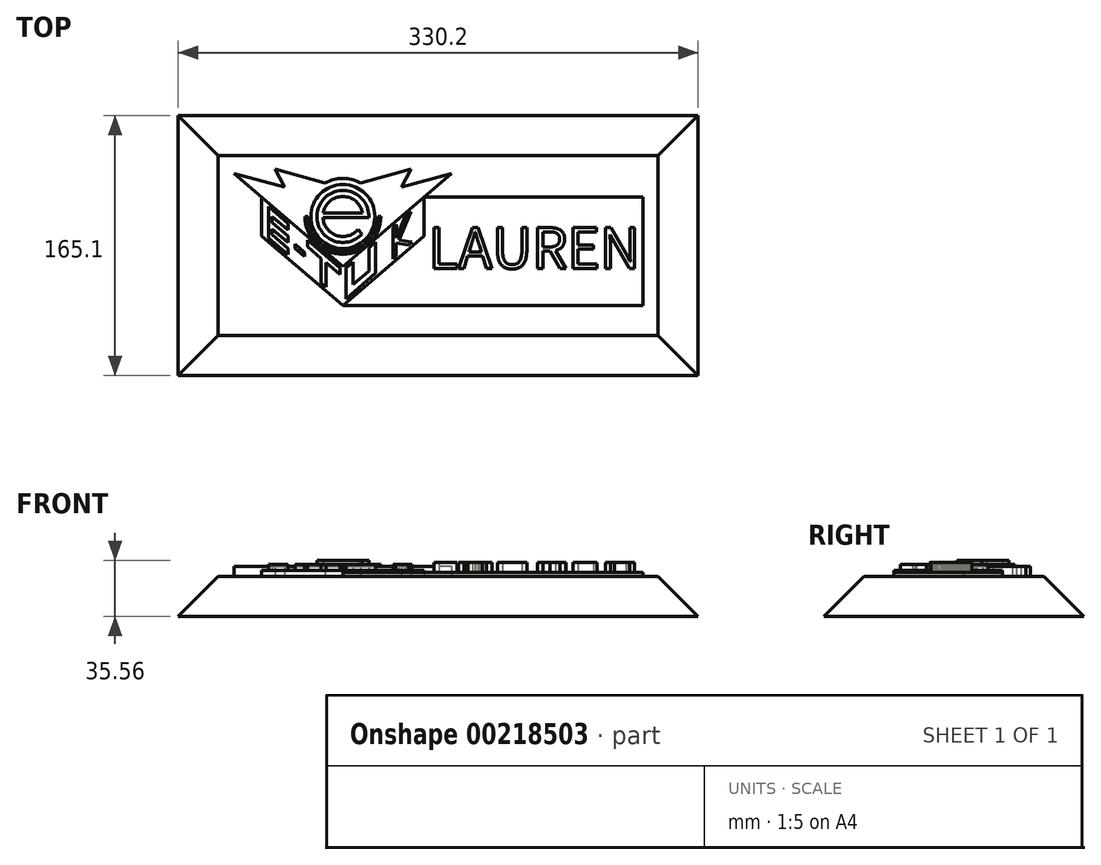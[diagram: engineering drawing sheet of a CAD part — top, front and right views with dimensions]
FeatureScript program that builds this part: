
annotation { "Feature Type Name" : "Feature", "Feature Type Description" : "" }
export const myFeature = defineFeature(function(context is Context, id is Id, definition is map)
    precondition{}
    {
        {
            var Q0;
            Q0=qCreatedBy(makeId("Top.planeOp"),FACE);
            var sketch = newSketch(context, id + "F0", { "sketchPlane" : qUnion([Q0])});
            skArc(sketch, "E0", {"start": v(12.53, 2.07) * mm, "mid": v(0, 12.7) * mm, "end": v(-12.53, 2.07) * mm});
            skArc(sketch, "E1", {"start": v(16.5, -0.78) * mm, "mid": v(-15.23, 6.37) * mm, "end": v(12.14, -11.18) * mm});
            skLineSegment(sketch, "E2", {"start": v(12.7, -0.78) * mm, "end": v(-12.68, -0.78) * mm});
            skLineSegment(sketch, "E3", {"start": v(-12.68, -0.78) * mm, "end": v(16.5, -0.78) * mm});
            skLineSegment(sketch, "E4", {"start": v(9.59, -8.33) * mm, "end": v(12.14, -11.18) * mm});
            skArc(sketch, "E5.trimOffspring", {"start": v(-12.68, -0.78) * mm, "mid": v(-4.08, -12.03) * mm, "end": v(9.59, -8.33) * mm});
            skLineSegment(sketch, "E6", {"start": v(-12.53, 2.07) * mm, "end": v(12.53, 2.07) * mm});
            skSolve(sketch);
        }
        {
            var Q0;
            Q0=makeQuery(id+"F0.imprint","IMPRINT",FACE,{"disambiguationData":[TD([[makeQuery(id+"F0.imprint","IMPRINT",EDGE,{"derivedFrom":sQuery(id+"F0.wireOp",EDGE,"E0")}),-1.0]])]});
            extrude(context, id + "F1", {"entities" : qUnion([Q0]), "depth" : 10.16 * mm});
        }
        {
            var Q0;
            Q0=qCreatedBy(makeId("Top.planeOp"),FACE);
            var sketch = newSketch(context, id + "F2", { "sketchPlane" : qUnion([Q0])});
            skCircle(sketch, "E7", {"center": v(0, 0) * mm, "radius": 20.32 * mm});
            skSolve(sketch);
        }
        {
            var Q0;
            Q0=qSketchRegion(id+"F2",true);
            extrude(context, id + "F3", {"entities" : qUnion([Q0]), "operationType" : NewBodyOperationType.ADD, "depth" : 7.62 * mm});
        }
        {
            var Q0;
            Q0=qCreatedBy(makeId("Top.planeOp"),FACE);
            var sketch = newSketch(context, id + "F4", { "sketchPlane" : qUnion([Q0])});
            skLineSegment(sketch, "E8", {"start": v(-69.02, 27.27) * mm, "end": v(-37.13, 18.72) * mm});
            skLineSegment(sketch, "E9", {"start": v(-37.13, 18.72) * mm, "end": v(-43.14, 30.14) * mm});
            skLineSegment(sketch, "E10", {"start": v(-43.14, 30.14) * mm, "end": v(-11.32, 21.31) * mm});
            skLineSegment(sketch, "E11", {"start": v(-69.02, 27.27) * mm, "end": v(0, -31.75) * mm});
            skLineSegment(sketch, "E12.MirrorCS", {"start": v(43.14, 30.14) * mm, "end": v(11.32, 21.31) * mm});
            skLineSegment(sketch, "E13.MirrorCS", {"start": v(69.02, 27.27) * mm, "end": v(0, -31.75) * mm});
            skLineSegment(sketch, "E14.MirrorCS", {"start": v(69.02, 27.27) * mm, "end": v(37.13, 18.72) * mm});
            skLineSegment(sketch, "E15.MirrorCS", {"start": v(37.13, 18.72) * mm, "end": v(43.14, 30.14) * mm});
            skArc(sketch, "E16.trimOffspring", {"start": v(11.32, 21.31) * mm, "mid": v(0, 24.13) * mm, "end": v(-11.32, 21.31) * mm});
            skSolve(sketch);
        }
        {
            var Q0;
            Q0=qSketchRegion(id+"F4",true);
            var Q1;
            Q1=makeQuery(id+"F2.imprint","IMPRINT",FACE,{"disambiguationData":[TD([[makeQuery(id+"F2.imprint","IMPRINT",EDGE,{"derivedFrom":sQuery(id+"F2.wireOp",EDGE,"E7")}),1.0]])]});
            extrude(context, id + "F5", {"entities" : qUnion([Q0, Q1]), "operationType" : NewBodyOperationType.ADD, "depth" : 6.35 * mm});
        }
        {
            var Q0;
            Q0=qCreatedBy(makeId("Top.planeOp"),FACE);
            var sketch = newSketch(context, id + "F6", { "sketchPlane" : qUnion([Q0])});
            skLineSegment(sketch, "E17", {"start": v(-51.6, -12.38) * mm, "end": v(0, -56.51) * mm});
            skLineSegment(sketch, "E18", {"start": v(0, -56.51) * mm, "end": v(51.6, -12.38) * mm});
            skLineSegment(sketch, "E19", {"start": v(-51.6, 12.38) * mm, "end": v(-51.6, -12.38) * mm});
            skLineSegment(sketch, "E20", {"start": v(51.6, 12.38) * mm, "end": v(51.6, -12.38) * mm});
            skLineSegment(sketch, "E21", {"start": v(-51.6, 12.38) * mm, "end": v(0, -31.75) * mm});
            skLineSegment(sketch, "E22", {"start": v(0, -31.75) * mm, "end": v(51.6, 12.38) * mm});
            skSolve(sketch);
        }
        {
            var Q0;
            Q0=qSketchRegion(id+"F6",true);
            extrude(context, id + "F7", {"entities" : qUnion([Q0]), "operationType" : NewBodyOperationType.ADD, "depth" : 3.8 * mm});
        }
        {
            var Q0;
            Q0=makeQuery(id+"F7.opExtrude","CAP_FACE",FACE,{"disambiguationData":[OSD([sQuery(id+"F6.wireOp",EDGE,"E17"),sQuery(id+"F6.wireOp",EDGE,"E18"),sQuery(id+"F6.wireOp",EDGE,"E19"),sQuery(id+"F6.wireOp",EDGE,"E20"),sQuery(id+"F6.wireOp",EDGE,"E21"),sQuery(id+"F6.wireOp",EDGE,"E22")])],"isStart":false});
            var sketch = newSketch(context, id + "F8", { "sketchPlane" : qUnion([Q0])});
            skPoint(sketch, "E23.startSnap0", {"position": v(-51.6, 0) * mm});
            skLineSegment(sketch, "E24", {"start": v(-51.6, -9.87) * mm, "end": v(-51.6, 9.87) * mm, "construction": true});
            skLineSegment(sketch, "E25", {"start": v(-47.26, 6.16) * mm, "end": v(-34.74, -4.55) * mm});
            skLineSegment(sketch, "E26", {"start": v(-34.74, -4.55) * mm, "end": v(-34.74, -8.63) * mm});
            skLineSegment(sketch, "E27", {"start": v(-34.74, -8.63) * mm, "end": v(-44.83, 0) * mm});
            skLineSegment(sketch, "E28", {"start": v(-44.83, 0) * mm, "end": v(-44.83, -3.75) * mm});
            skLineSegment(sketch, "E29", {"start": v(-44.83, -3.75) * mm, "end": v(-34.74, -12.38) * mm});
            skLineSegment(sketch, "E30", {"start": v(-34.74, -12.38) * mm, "end": v(-34.74, -16.46) * mm});
            skLineSegment(sketch, "E31", {"start": v(-34.74, -16.46) * mm, "end": v(-44.83, -7.83) * mm});
            skLineSegment(sketch, "E32", {"start": v(-44.83, -7.83) * mm, "end": v(-44.83, -11.58) * mm});
            skLineSegment(sketch, "E33", {"start": v(-44.83, -11.58) * mm, "end": v(-34.74, -20.21) * mm});
            skLineSegment(sketch, "E34", {"start": v(-34.74, -20.21) * mm, "end": v(-34.74, -24.3) * mm});
            skLineSegment(sketch, "E35", {"start": v(-34.74, -24.3) * mm, "end": v(-47.26, -13.59) * mm});
            skLineSegment(sketch, "E36", {"start": v(-47.26, 6.16) * mm, "end": v(-47.26, -13.59) * mm});
            skLineSegment(sketch, "E37", {"start": v(-30.38, -20.21) * mm, "end": v(-30.38, -17.65) * mm});
            skLineSegment(sketch, "E38", {"start": v(-30.38, -17.65) * mm, "end": v(-24.17, -22.96) * mm});
            skLineSegment(sketch, "E39", {"start": v(-24.17, -22.96) * mm, "end": v(-24.17, -25.53) * mm});
            skLineSegment(sketch, "E40", {"start": v(-24.17, -25.53) * mm, "end": v(-30.38, -20.21) * mm});
            skLineSegment(sketch, "E41", {"start": v(-22.38, -15.12) * mm, "end": v(-1.9, -32.63) * mm});
            skLineSegment(sketch, "E42", {"start": v(-1.9, -32.63) * mm, "end": v(-1.9, -36.71) * mm});
            skLineSegment(sketch, "E43", {"start": v(-1.9, -36.71) * mm, "end": v(-10.6, -29.28) * mm});
            skLineSegment(sketch, "E44", {"start": v(-10.6, -29.28) * mm, "end": v(-10.6, -44.95) * mm});
            skLineSegment(sketch, "E45", {"start": v(-10.6, -44.95) * mm, "end": v(-13.7, -42.3) * mm});
            skLineSegment(sketch, "E46", {"start": v(-13.7, -42.3) * mm, "end": v(-13.7, -26.63) * mm});
            skLineSegment(sketch, "E47", {"start": v(-13.7, -26.63) * mm, "end": v(-22.38, -19.2) * mm});
            skLineSegment(sketch, "E48", {"start": v(-22.38, -19.2) * mm, "end": v(-22.38, -15.12) * mm});
            skLineSegment(sketch, "E49", {"start": v(1.9, -32.62) * mm, "end": v(6.3, -28.86) * mm});
            skLineSegment(sketch, "E50", {"start": v(6.3, -28.86) * mm, "end": v(6.3, -43.26) * mm});
            skLineSegment(sketch, "E51", {"start": v(6.3, -43.26) * mm, "end": v(16.5, -34.54) * mm});
            skLineSegment(sketch, "E52", {"start": v(16.5, -34.54) * mm, "end": v(16.5, -20.14) * mm});
            skLineSegment(sketch, "E53", {"start": v(16.5, -20.14) * mm, "end": v(20.85, -16.3) * mm});
            skLineSegment(sketch, "E54", {"start": v(20.85, -16.3) * mm, "end": v(20.85, -36.06) * mm});
            skLineSegment(sketch, "E55", {"start": v(20.85, -36.06) * mm, "end": v(1.9, -52.37) * mm});
            skLineSegment(sketch, "E56", {"start": v(1.9, -52.37) * mm, "end": v(1.9, -32.62) * mm});
            skLineSegment(sketch, "E57", {"start": v(31.73, -7.12) * mm, "end": v(31.73, -27.15) * mm});
            skLineSegment(sketch, "E58", {"start": v(31.73, -27.15) * mm, "end": v(33.91, -25.22) * mm});
            skLineSegment(sketch, "E59", {"start": v(33.91, -25.22) * mm, "end": v(33.91, -16.82) * mm});
            skLineSegment(sketch, "E60", {"start": v(33.94, -13.64) * mm, "end": v(33.94, -5.23) * mm});
            skLineSegment(sketch, "E61", {"start": v(33.94, -5.23) * mm, "end": v(31.73, -7.12) * mm});
            skLineSegment(sketch, "E62", {"start": v(41.79, -18.27) * mm, "end": v(44, -16.38) * mm});
            skLineSegment(sketch, "E63", {"start": v(33.94, -13.64) * mm, "end": v(39.5, 0) * mm});
            skLineSegment(sketch, "E64", {"start": v(33.91, -16.82) * mm, "end": v(41.79, -18.27) * mm});
            skLineSegment(sketch, "E65", {"start": v(44, -16.38) * mm, "end": v(35.85, -14.87) * mm});
            skLineSegment(sketch, "E66", {"start": v(35.85, -14.87) * mm, "end": v(43.2, 3.16) * mm});
            skLineSegment(sketch, "E67", {"start": v(39.5, 0) * mm, "end": v(43.2, 3.16) * mm});
            skSolve(sketch);
        }
        {
            var Q0;
            Q0=qSketchRegion(id+"F8",true);
            extrude(context, id + "F9", {"entities" : qUnion([Q0]), "operationType" : NewBodyOperationType.ADD, "depth" : 3.8 * mm});
        }
        {
            var Q0;
            Q0=makeQuery(id+"F5.boolean.opBoolean","MERGE",FACE,{"derivedFrom":[makeQuery(id+"F5.opExtrude","CAP_FACE",FACE,{"disambiguationData":[OSD([sQuery(id+"F2.wireOp",EDGE,"E7")])],"isStart":false}),makeQuery(id+"F5.opExtrude","CAP_FACE",FACE,{"disambiguationData":[OSD([sQuery(id+"F4.wireOp",EDGE,"E8"),sQuery(id+"F4.wireOp",EDGE,"E9"),sQuery(id+"F4.wireOp",EDGE,"E10"),sQuery(id+"F4.wireOp",EDGE,"E11"),sQuery(id+"F4.wireOp",EDGE,"E13.MirrorCS"),sQuery(id+"F4.wireOp",EDGE,"E14.MirrorCS"),sQuery(id+"F4.wireOp",EDGE,"E12.MirrorCS"),sQuery(id+"F4.wireOp",EDGE,"E15.MirrorCS"),sQuery(id+"F4.wireOp",EDGE,"E16.trimOffspring")])],"isStart":false})]});
            var sketch = newSketch(context, id + "F10", { "sketchPlane" : qUnion([Q0])});
            skArc(sketch, "E68", {"start": v(-24.13, 0) * mm, "mid": v(0, -24.13) * mm, "end": v(24.13, 0) * mm});
            skArc(sketch, "E69", {"start": v(-22.23, 0) * mm, "mid": v(0, -22.23) * mm, "end": v(22.23, 0) * mm});
            skLineSegment(sketch, "E70", {"start": v(-24.13, 0) * mm, "end": v(-22.23, 0) * mm});
            skLineSegment(sketch, "E71", {"start": v(24.13, 0) * mm, "end": v(22.23, 0) * mm});
            skSolve(sketch);
        }
        {
            var Q0;
            Q0=qSketchRegion(id+"F10",true);
            extrude(context, id + "F11", {"entities" : qUnion([Q0]), "operationType" : NewBodyOperationType.ADD, "depth" : 1.27 * mm});
        }
        {
            var Q0;
            {var subQ0=sQuery(id+"F2.wireOp",EDGE,"E7");Q0=makeQuery(id+"F7.boolean.opBoolean","MERGE",FACE,{"derivedFrom":[makeQuery(id+"F5.boolean.opBoolean","MERGE",FACE,{"derivedFrom":[makeQuery(id+"F3.boolean.opBoolean","MERGE",FACE,{"derivedFrom":[makeQuery(id+"F1.opExtrude","CAP_FACE",FACE,{"disambiguationData":[OSD([sQuery(id+"F0.wireOp",EDGE,"E0"),sQuery(id+"F0.wireOp",EDGE,"E1"),sQuery(id+"F0.wireOp",EDGE,"E3"),sQuery(id+"F0.wireOp",EDGE,"E4"),sQuery(id+"F0.wireOp",EDGE,"E5.trimOffspring"),sQuery(id+"F0.wireOp",EDGE,"E6")])],"isStart":true}),makeQuery(id+"F3.opExtrude","CAP_FACE",FACE,{"disambiguationData":[OSD([subQ0])],"isStart":true})]}),makeQuery(id+"F5.opExtrude","CAP_FACE",FACE,{"disambiguationData":[OSD([subQ0])],"isStart":true}),makeQuery(id+"F5.opExtrude","CAP_FACE",FACE,{"disambiguationData":[OSD([sQuery(id+"F4.wireOp",EDGE,"E8"),sQuery(id+"F4.wireOp",EDGE,"E9"),sQuery(id+"F4.wireOp",EDGE,"E10"),sQuery(id+"F4.wireOp",EDGE,"E11"),sQuery(id+"F4.wireOp",EDGE,"E13.MirrorCS"),sQuery(id+"F4.wireOp",EDGE,"E14.MirrorCS"),sQuery(id+"F4.wireOp",EDGE,"E12.MirrorCS"),sQuery(id+"F4.wireOp",EDGE,"E15.MirrorCS"),sQuery(id+"F4.wireOp",EDGE,"E16.trimOffspring")])],"isStart":true})]}),makeQuery(id+"F7.opExtrude","CAP_FACE",FACE,{"disambiguationData":[OSD([sQuery(id+"F6.wireOp",EDGE,"E17"),sQuery(id+"F6.wireOp",EDGE,"E18"),sQuery(id+"F6.wireOp",EDGE,"E19"),sQuery(id+"F6.wireOp",EDGE,"E20"),sQuery(id+"F6.wireOp",EDGE,"E21"),sQuery(id+"F6.wireOp",EDGE,"E22")])],"isStart":true})]});}
            var sketch = newSketch(context, id + "F12", { "sketchPlane" : qUnion([Q0])});
            skLineSegment(sketch, "E72.bottom", {"start": v(0, 56.51) * mm, "end": v(190.5, 56.51) * mm});
            skLineSegment(sketch, "E72.right", {"start": v(190.5, 56.51) * mm, "end": v(190.5, -12.38) * mm});
            skLineSegment(sketch, "E73", {"start": v(51.6, -12.38) * mm, "end": v(190.5, -12.38) * mm});
            skLineSegment(sketch, "E74", {"start": v(0, 56.51) * mm, "end": v(51.6, 12.38) * mm});
            skLineSegment(sketch, "E75", {"start": v(51.6, 12.38) * mm, "end": v(51.6, -12.38) * mm});
            skSolve(sketch);
        }
        {
            var Q0;
            Q0=qSketchRegion(id+"F12",true);
            extrude(context, id + "F13", {"entities" : qUnion([Q0]), "operationType" : NewBodyOperationType.ADD, "oppositeDirection" : true, "depth" : 2.54 * mm});
        }
        {
            var Q0;
            Q0=makeQuery(id+"F13.opExtrude","CAP_FACE",FACE,{"disambiguationData":[OSD([sQuery(id+"F12.wireOp",EDGE,"E72.bottom"),sQuery(id+"F12.wireOp",EDGE,"E72.right"),sQuery(id+"F12.wireOp",EDGE,"E73"),sQuery(id+"F12.wireOp",EDGE,"E74"),sQuery(id+"F12.wireOp",EDGE,"E75")])],"isStart":false});
            var sketch = newSketch(context, id + "F14", { "sketchPlane" : qUnion([Q0])});
            skLineSegment(sketch, "E76", {"start": v(51.6, 12.38) * mm, "end": v(51.6, -56.51) * mm, "construction": true});
            skLineSegment(sketch, "E77", {"start": v(51.6, -56.51) * mm, "end": v(190.5, -56.51) * mm, "construction": true});
            skLineSegment(sketch, "E78", {"start": v(190.5, -56.51) * mm, "end": v(190.5, 12.38) * mm, "construction": true});
            skLineSegment(sketch, "E79", {"start": v(190.5, 12.38) * mm, "end": v(51.6, 12.38) * mm, "construction": true});
            skPoint(sketch, "E80.startSnap0", {"position": v(51.6, 0) * mm});
            skPoint(sketch, "E80.endSnap0", {"position": v(51.6, 0) * mm});
            skLineSegment(sketch, "E81", {"start": v(187.28, -32.97) * mm, "end": v(54.25, -32.97) * mm, "construction": true});
            skLineSegment(sketch, "E82", {"start": v(161.5, -7.57) * mm, "end": v(54.25, -7.57) * mm, "construction": true});
            skText(sketch, "E83", { "text": "LAUREN", "fontName": "NotoSansCJKkr-Regular.otf"});
            const initialGuessF14  = {"E83": [0.05425, -0.03297, 1, 0, 0.0254]};
            skSetInitialGuess(sketch, initialGuessF14);
            skSolve(sketch);
        }
        {
            var Q0;
            Q0=qSketchRegion(id+"F14",true);
            extrude(context, id + "F15", {"entities" : qUnion([Q0]), "operationType" : NewBodyOperationType.ADD, "depth" : 6.35 * mm});
        }
        {
            var Q0;
            Q0=makeQuery(id+"F13.opExtrude","CAP_FACE",FACE,{"disambiguationData":[OSD([sQuery(id+"F12.wireOp",EDGE,"E72.bottom"),sQuery(id+"F12.wireOp",EDGE,"E72.right"),sQuery(id+"F12.wireOp",EDGE,"E73"),sQuery(id+"F12.wireOp",EDGE,"E74"),sQuery(id+"F12.wireOp",EDGE,"E75")])],"isStart":true});
            var sketch = newSketch(context, id + "F16", { "sketchPlane" : qUnion([Q0])});
            skLineSegment(sketch, "E84.bottom", {"start": v(-79.18, -38.74) * mm, "end": v(200.22, -38.74) * mm});
            skLineSegment(sketch, "E84.top", {"start": v(-79.18, 75.56) * mm, "end": v(200.22, 75.56) * mm});
            skLineSegment(sketch, "E84.left", {"start": v(-79.18, -38.74) * mm, "end": v(-79.18, 75.56) * mm});
            skLineSegment(sketch, "E84.right", {"start": v(200.22, -38.74) * mm, "end": v(200.22, 75.56) * mm});
            skSolve(sketch);
        }
        {
            var Q0;
            Q0=qSketchRegion(id+"F16",true);
            extrude(context, id + "F17", {"entities" : qUnion([Q0]), "operationType" : NewBodyOperationType.ADD, "depth" : 25.4 * mm, "hasDraft" : true, "draftAngle" : 45 * degree});
        }
    });
